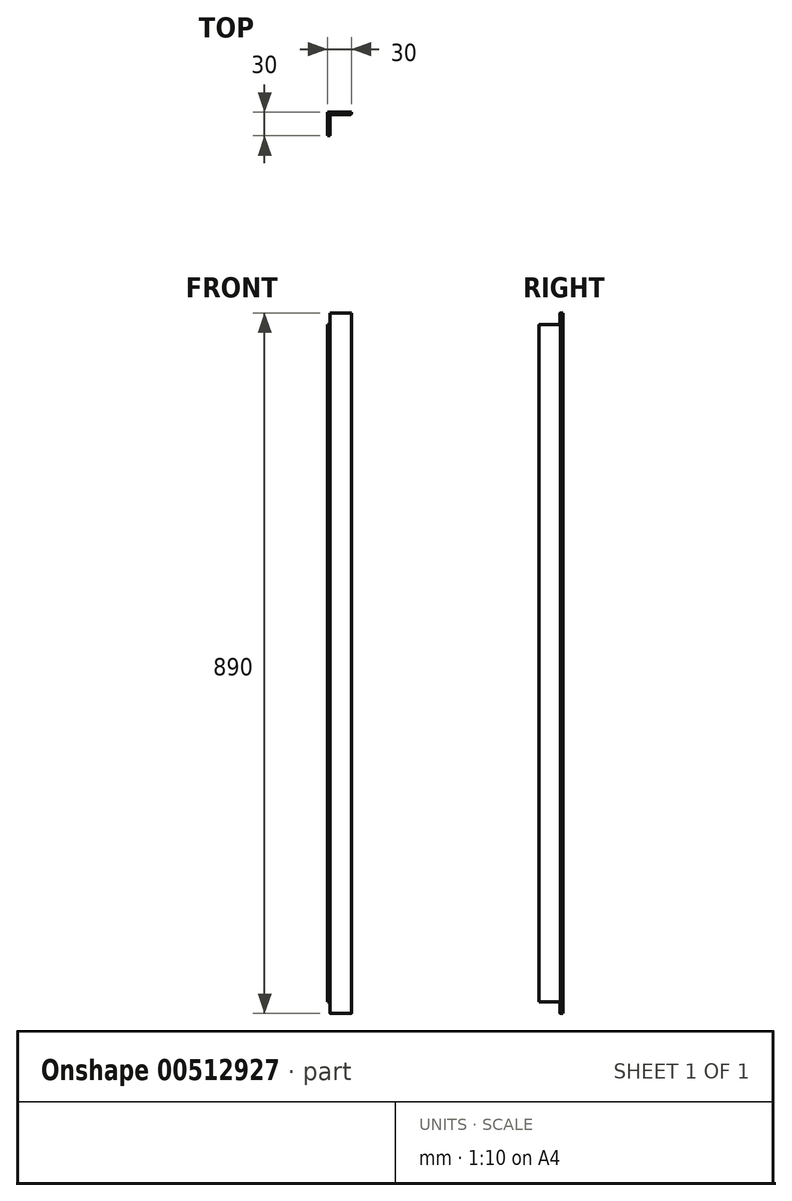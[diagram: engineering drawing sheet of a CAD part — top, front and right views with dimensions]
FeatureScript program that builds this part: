
annotation { "Feature Type Name" : "Feature", "Feature Type Description" : "" }
export const myFeature = defineFeature(function(context is Context, id is Id, definition is map)
    precondition{}
    {
        {
            var Q0;
            Q0=qCreatedBy(makeId("Top.planeOp"),FACE);
            var sketch = newSketch(context, id + "F0", { "sketchPlane" : qUnion([Q0])});
            skLineSegment(sketch, "E0.0", {"start": v(-0.03, 0.03) * mm, "end": v(-0.03, -29.97) * mm});
            skLineSegment(sketch, "E0.1", {"start": v(-0.03, -29.97) * mm, "end": v(1.97, -29.97) * mm});
            skLineSegment(sketch, "E0.2", {"start": v(2.97, -28.97) * mm, "end": v(2.97, -3.97) * mm});
            skLineSegment(sketch, "E0.3", {"start": v(3.97, -2.97) * mm, "end": v(28.97, -2.97) * mm});
            skLineSegment(sketch, "E0.4", {"start": v(29.97, -1.97) * mm, "end": v(29.97, 0.03) * mm});
            skLineSegment(sketch, "E0.5", {"start": v(29.97, 0.03) * mm, "end": v(-0.03, 0.03) * mm});
            skPoint(sketch, "E0.6", {"position": v(2.97, -2.97) * mm});
            skArc(sketch, "E0.7", {"start": v(3.97, -2.97) * mm, "mid": v(3.26, -3.26) * mm, "end": v(2.97, -3.97) * mm});
            skPoint(sketch, "E0.8", {"position": v(2.97, -29.97) * mm});
            skArc(sketch, "E0.9", {"start": v(1.97, -29.97) * mm, "mid": v(2.68, -29.68) * mm, "end": v(2.97, -28.97) * mm});
            skPoint(sketch, "E0.10", {"position": v(29.97, -2.97) * mm});
            skArc(sketch, "E0.11", {"start": v(28.97, -2.97) * mm, "mid": v(29.68, -2.68) * mm, "end": v(29.97, -1.97) * mm});
            skSolve(sketch);
        }
        {
            var Q0;
            Q0 = qSketchRegion(id + "F0", true);
            extrude(context, id + "F1", {"entities" : qUnion([Q0]), "depth" : 920 * mm, "offsetDistance" : 25 * mm});
        }
        {
            var Q0;
            Q0=qCreatedBy(makeId("Front.planeOp"),FACE);
            var sketch = newSketch(context, id + "F2", { "sketchPlane" : qUnion([Q0])});
            skLineSegment(sketch, "E1", {"start": v(219.42, 460) * mm, "end": v(-159.48, 460) * mm, "construction": true});
            skLineSegment(sketch, "E2.bottom", {"start": v(3, -11.3) * mm, "end": v(35.35, -11.3) * mm});
            skLineSegment(sketch, "E2.top", {"start": v(3, 15) * mm, "end": v(35.35, 15) * mm});
            skLineSegment(sketch, "E2.left", {"start": v(3, -11.3) * mm, "end": v(3, 15) * mm});
            skLineSegment(sketch, "E2.right", {"start": v(35.35, -11.3) * mm, "end": v(35.35, 15) * mm});
            skLineSegment(sketch, "E3.MirrorCS", {"start": v(3, 931.3) * mm, "end": v(35.35, 931.3) * mm});
            skLineSegment(sketch, "E4.MirrorCS", {"start": v(3, 905) * mm, "end": v(35.35, 905) * mm});
            skLineSegment(sketch, "E5.MirrorCS", {"start": v(35.35, 931.3) * mm, "end": v(35.35, 905) * mm});
            skLineSegment(sketch, "E6.MirrorCS", {"start": v(3, 931.3) * mm, "end": v(3, 905) * mm});
            skSolve(sketch);
        }
        {
            var Q0;
            Q0 = qSketchRegion(id + "F2", true);
            extrude(context, id + "F3", {"entities" : qUnion([Q0]), "operationType" : NewBodyOperationType.REMOVE, "depth" : 25 * mm, "offsetDistance" : 25 * mm, "hasSecondDirection" : true, "secondDirectionOppositeDirection" : true, "secondDirectionDepth" : 25 * mm});
        }
        {
            var Q0;
            Q0=qCreatedBy(makeId("Right.planeOp"),FACE);
            var sketch = newSketch(context, id + "F4", { "sketchPlane" : qUnion([Q0])});
            skLineSegment(sketch, "E7", {"start": v(215.77, 460) * mm, "end": v(-215.72, 460) * mm, "construction": true});
            skLineSegment(sketch, "E8.bottom", {"start": v(-62.4, -41.54) * mm, "end": v(30.88, -41.54) * mm});
            skLineSegment(sketch, "E8.top", {"start": v(-62.4, 30) * mm, "end": v(30.88, 30) * mm});
            skLineSegment(sketch, "E8.left", {"start": v(-62.4, -41.54) * mm, "end": v(-62.4, 30) * mm});
            skLineSegment(sketch, "E8.right", {"start": v(30.88, -41.54) * mm, "end": v(30.88, 30) * mm});
            skLineSegment(sketch, "E9.MirrorCS", {"start": v(30.88, 961.54) * mm, "end": v(30.88, 890) * mm});
            skLineSegment(sketch, "E10.MirrorCS", {"start": v(-62.4, 961.54) * mm, "end": v(-62.4, 890) * mm});
            skLineSegment(sketch, "E11.MirrorCS", {"start": v(-62.4, 961.54) * mm, "end": v(30.88, 961.54) * mm});
            skLineSegment(sketch, "E12.MirrorCS", {"start": v(-62.4, 890) * mm, "end": v(30.88, 890) * mm});
            skSolve(sketch);
        }
        {
            var Q0;
            Q0 = qSketchRegion(id + "F4", true);
            extrude(context, id + "F5", {"entities" : qUnion([Q0]), "operationType" : NewBodyOperationType.REMOVE, "depth" : 3 * mm, "offsetDistance" : 25 * mm, "hasSecondDirection" : true, "secondDirectionOppositeDirection" : true, "secondDirectionDepth" : 25 * mm});
        }
    });
